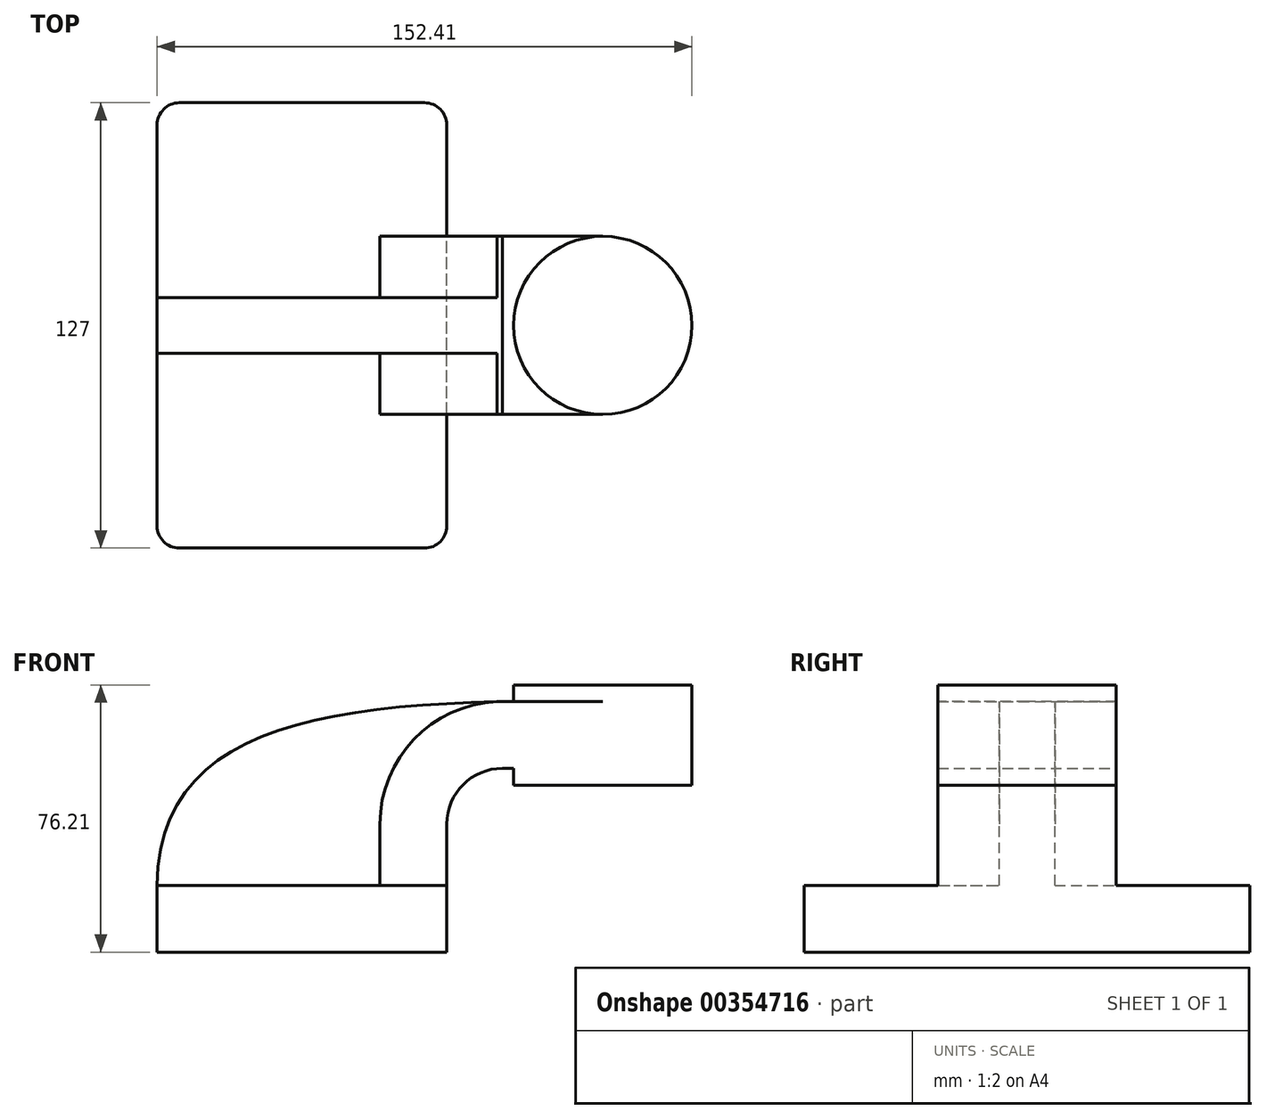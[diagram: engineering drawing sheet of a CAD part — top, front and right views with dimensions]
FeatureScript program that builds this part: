
annotation { "Feature Type Name" : "Feature", "Feature Type Description" : "" }
export const myFeature = defineFeature(function(context is Context, id is Id, definition is map)
    precondition{}
    {
        {
            var Q0;
            Q0=qCreatedBy(makeId("Front.planeOp"),FACE);
            var sketch = newSketch(context, id + "F0", { "sketchPlane" : qUnion([Q0])});
            skLineSegment(sketch, "E0.bottom", {"start": v(-41.28, -9.53) * mm, "end": v(41.28, -9.53) * mm});
            skLineSegment(sketch, "E0.top", {"start": v(-41.28, 9.52) * mm, "end": v(41.28, 9.52) * mm});
            skLineSegment(sketch, "E0.left", {"start": v(-41.28, -9.53) * mm, "end": v(-41.28, 9.52) * mm});
            skLineSegment(sketch, "E0.right", {"start": v(41.28, -9.53) * mm, "end": v(41.28, 9.52) * mm});
            skPoint(sketch, "E0.middle", {"position": v(0, 0) * mm});
            skLineSegment(sketch, "E1.bottom", {"start": v(111.12, 38.1) * mm, "end": v(60.32, 38.1) * mm});
            skLineSegment(sketch, "E1.top", {"start": v(111.12, 66.67) * mm, "end": v(60.32, 66.67) * mm});
            skLineSegment(sketch, "E1.left", {"start": v(111.12, 38.1) * mm, "end": v(111.12, 66.68) * mm});
            skLineSegment(sketch, "E1.right", {"start": v(60.32, 38.1) * mm, "end": v(60.32, 66.68) * mm});
            skPoint(sketch, "E1.middle", {"position": v(85.72, 52.39) * mm});
            skLineSegment(sketch, "E2", {"start": v(41.27, 9.52) * mm, "end": v(41.27, 27) * mm});
            skArc(sketch, "E3", {"start": v(41.27, 27) * mm, "mid": v(45.92, 38.23) * mm, "end": v(57.15, 42.88) * mm});
            skLineSegment(sketch, "E4", {"start": v(57.15, 42.88) * mm, "end": v(75.4, 42.88) * mm});
            skLineSegment(sketch, "E5.0", {"start": v(57.15, 61.93) * mm, "end": v(85.72, 61.93) * mm});
            skArc(sketch, "E5.1", {"start": v(22.23, 27) * mm, "mid": v(32.45, 51.7) * mm, "end": v(57.15, 61.93) * mm});
            skLineSegment(sketch, "E5.2", {"start": v(22.22, 9.52) * mm, "end": v(22.22, 27) * mm});
            skLineSegment(sketch, "E6", {"start": v(85.72, 38.1) * mm, "end": v(85.72, 66.67) * mm});
            skFitSpline(sketch, "E7", {"points": [v(-41.28, 9.52) * mm, v(57.15, 61.93) * mm], "startDerivative": vector(1.01, 126.91) * mm, "endDerivative": vector(171.45, 3.73) * mm});
            skSolve(sketch);
        }
        {
            var Q0;
            Q0=makeQuery(id+"F0.imprint","IMPRINT",FACE,{"disambiguationData":[TD([[makeQuery(id+"F0.imprint","IMPRINT",EDGE,{"derivedFrom":sQuery(id+"F0.wireOp",EDGE,"E0.bottom")}),1.0]])]});
            extrude(context, id + "F1", {"entities" : qUnion([Q0]), "endBound" : BoundingType.SYMMETRIC, "depth" : 127 * mm});
        }
        {
            var Q0;
            {var subQ1=sQuery(id+"F0.wireOp",EDGE,"E2");Q0=makeQuery(id+"F0.imprint","IMPRINT",FACE,{"disambiguationData":[TD([[makeQuery(id+"F0.imprint","IMPRINT",EDGE,{"derivedFrom":subQ1}),1.0]])]});}
            var Q1;
            {var subQ3=sQuery(id+"F0.wireOp",EDGE,"E1.right");var subQ5=sQuery(id+"F0.wireOp",EDGE,"E1.bottom");var subQ6=makeQuery(id+"F0.imprint","INTERSECT",VERTEX,{"derivedFrom":[subQ5,subQ3]});Q1=makeQuery(id+"F0.imprint","IMPRINT",FACE,{"disambiguationData":[TD([[makeQuery(id+"F0.imprint","IMPRINT",EDGE,{"disambiguationData":[TD([[subQ6,1.0]])],"derivedFrom":subQ5}),-1.0]])]});}
            extrude(context, id + "F2", {"entities" : qUnion([Q0, Q1]), "operationType" : NewBodyOperationType.ADD, "endBound" : BoundingType.SYMMETRIC, "depth" : 50.8 * mm});
        }
        {
            var Q0;
            {var subQ3=sQuery(id+"F0.wireOp",EDGE,"E5.2");Q0=makeQuery(id+"F0.imprint","IMPRINT",FACE,{"disambiguationData":[TD([[makeQuery(id+"F0.imprint","IMPRINT",EDGE,{"derivedFrom":subQ3}),1.0]])]});}
            extrude(context, id + "F3", {"entities" : qUnion([Q0]), "operationType" : NewBodyOperationType.ADD, "endBound" : BoundingType.SYMMETRIC, "depth" : 15.88 * mm});
        }
        {
            var Q0;
            {var subQ4=sQuery(id+"F0.wireOp",EDGE,"E1.left");Q0=makeQuery(id+"F0.imprint","IMPRINT",FACE,{"disambiguationData":[TD([[makeQuery(id+"F0.imprint","IMPRINT",EDGE,{"derivedFrom":subQ4}),1.0]])]});}
            var Q1;
            Q1=sQuery(id+"F0.wireOp",EDGE,"E6");
            revolve(context, id + "F4", {"operationType" : NewBodyOperationType.ADD, "entities" : qUnion([Q0]), "axis" : qUnion([Q1]), "revolveType" : RevolveType.FULL});
        }
        {
            var Q0;
            Q0=makeQuery(id+"F1.opExtrude","CAP_EDGE",EDGE,{"disambiguationData":[OSD([sQuery(id+"F0.wireOp",EDGE,"E0.right")])],"isStart":false});
            var Q1;
            Q1=makeQuery(id+"F1.opExtrude","CAP_EDGE",EDGE,{"disambiguationData":[OSD([sQuery(id+"F0.wireOp",EDGE,"E0.left")])],"isStart":false});
            var Q2;
            Q2=makeQuery(id+"F1.opExtrude","CAP_EDGE",EDGE,{"disambiguationData":[OSD([sQuery(id+"F0.wireOp",EDGE,"E0.right")])],"isStart":true});
            var Q3;
            Q3=makeQuery(id+"F1.opExtrude","CAP_EDGE",EDGE,{"disambiguationData":[OSD([sQuery(id+"F0.wireOp",EDGE,"E0.left")])],"isStart":true});
            fillet(context, id + "F5", {"entities" : qUnion([Q0, Q1, Q2, Q3]), "radius" : 6.35 * mm, "tangentPropagation" : true, "allowEdgeOverflow" : false});
        }
    });
